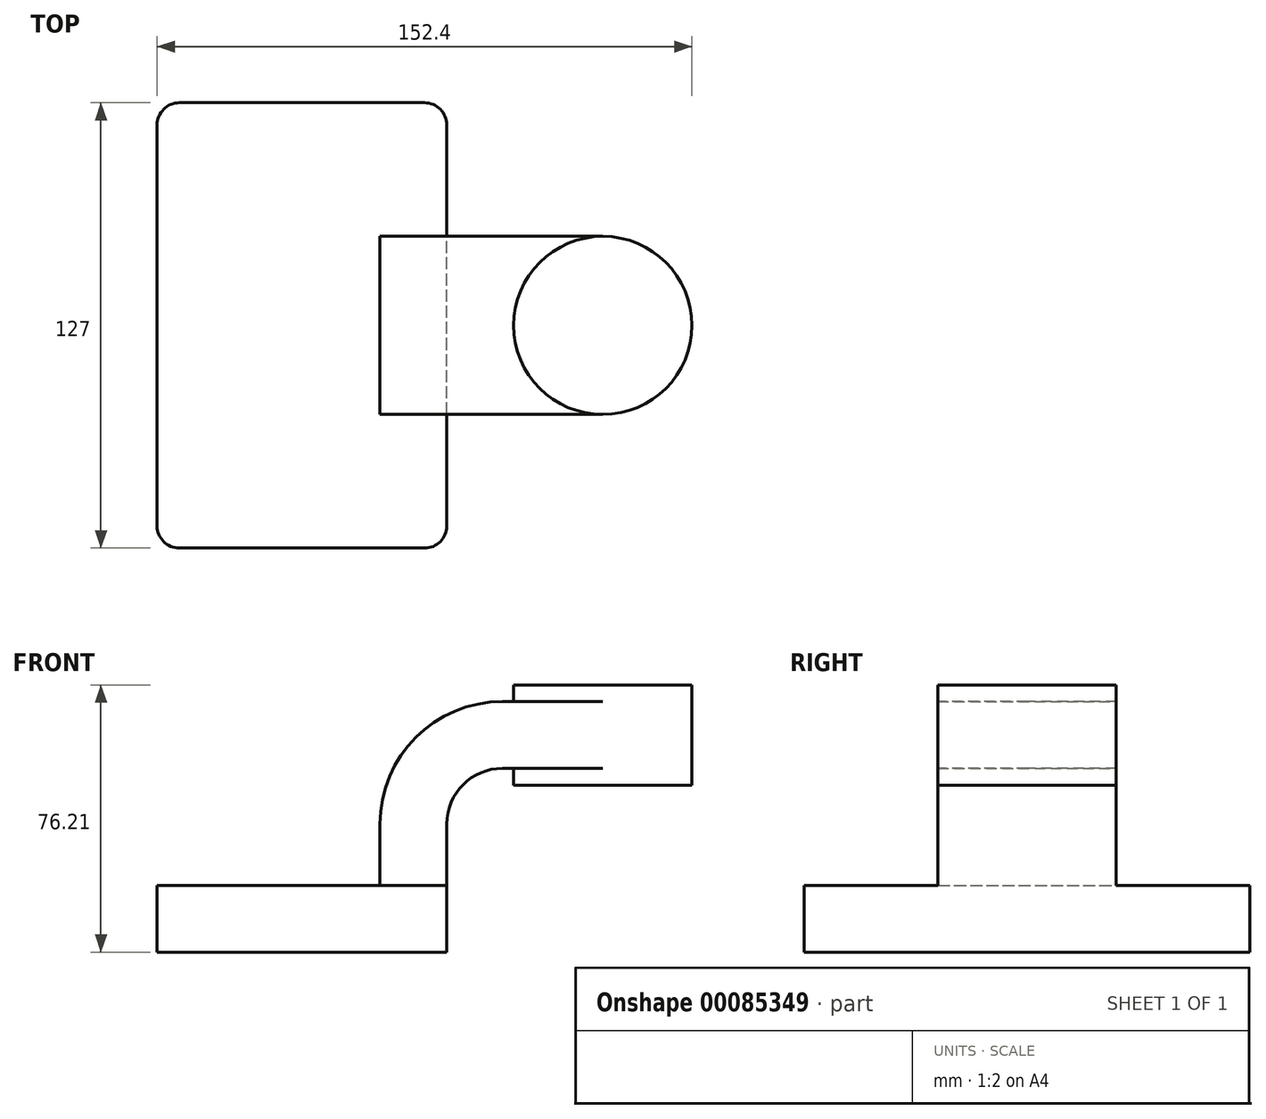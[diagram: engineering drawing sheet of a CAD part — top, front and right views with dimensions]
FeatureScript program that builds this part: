
annotation { "Feature Type Name" : "Feature", "Feature Type Description" : "" }
export const myFeature = defineFeature(function(context is Context, id is Id, definition is map)
    precondition{}
    {
        {
            var Q0;
            Q0=qCreatedBy(makeId("Front.planeOp"),FACE);
            var sketch = newSketch(context, id + "F0", { "sketchPlane" : qUnion([Q0])});
            skLineSegment(sketch, "E0.bottom", {"start": v(41.28, -9.52) * mm, "end": v(-41.28, -9.53) * mm});
            skLineSegment(sketch, "E0.top", {"start": v(41.28, 9.53) * mm, "end": v(-41.28, 9.53) * mm});
            skLineSegment(sketch, "E0.left", {"start": v(41.28, -9.52) * mm, "end": v(41.28, 9.53) * mm});
            skLineSegment(sketch, "E0.right", {"start": v(-41.28, -9.53) * mm, "end": v(-41.28, 9.53) * mm});
            skPoint(sketch, "E0.middle", {"position": v(0, 0) * mm});
            skLineSegment(sketch, "E1.bottom", {"start": v(60.33, 38.1) * mm, "end": v(111.12, 38.1) * mm});
            skLineSegment(sketch, "E1.top", {"start": v(60.32, 66.68) * mm, "end": v(111.12, 66.68) * mm});
            skLineSegment(sketch, "E1.left", {"start": v(60.33, 38.1) * mm, "end": v(60.32, 66.68) * mm});
            skLineSegment(sketch, "E1.right", {"start": v(111.12, 38.1) * mm, "end": v(111.12, 66.68) * mm});
            skPoint(sketch, "E1.middle", {"position": v(85.72, 52.39) * mm});
            skLineSegment(sketch, "E2", {"start": v(41.28, 9.53) * mm, "end": v(41.28, 27) * mm});
            skArc(sketch, "E3", {"start": v(41.27, 27) * mm, "mid": v(45.92, 38.23) * mm, "end": v(57.15, 42.88) * mm});
            skLineSegment(sketch, "E4", {"start": v(57.15, 42.88) * mm, "end": v(85.72, 42.88) * mm});
            skLineSegment(sketch, "E5.0", {"start": v(57.15, 61.93) * mm, "end": v(85.72, 61.93) * mm});
            skArc(sketch, "E5.1", {"start": v(22.23, 27) * mm, "mid": v(32.45, 51.7) * mm, "end": v(57.15, 61.93) * mm});
            skLineSegment(sketch, "E5.2", {"start": v(22.22, 9.53) * mm, "end": v(22.22, 27) * mm});
            skLineSegment(sketch, "E6", {"start": v(85.72, 38.1) * mm, "end": v(85.72, 66.68) * mm});
            skFitSpline(sketch, "E7", {"points": [v(-41.28, 9.53) * mm, v(57.15, 61.93) * mm], "startDerivative": vector(0, 117.26) * mm, "endDerivative": vector(131.4, 0) * mm});
            skPoint(sketch, "E8", {"position": v(-41.28, 0) * mm});
            skSolve(sketch);
        }
        {
            var Q0;
            Q0=makeQuery(id+"F0.imprint","IMPRINT",FACE,{"disambiguationData":[TD([[makeQuery(id+"F0.imprint","IMPRINT",EDGE,{"derivedFrom":sQuery(id+"F0.wireOp",EDGE,"E0.bottom")}),-1.0]])]});
            extrude(context, id + "F1", {"entities" : qUnion([Q0]), "endBound" : BoundingType.SYMMETRIC, "depth" : 127 * mm});
        }
        {
            var Q0;
            {var subQ1=sQuery(id+"F0.wireOp",EDGE,"E2");Q0=makeQuery(id+"F0.imprint","IMPRINT",FACE,{"disambiguationData":[TD([[makeQuery(id+"F0.imprint","IMPRINT",EDGE,{"derivedFrom":subQ1}),1.0]])]});}
            var Q1;
            {var subQ0=sQuery(id+"F0.wireOp",EDGE,"E4");var subQ1=sQuery(id+"F0.wireOp",EDGE,"E1.left");var subQ2=makeQuery(id+"F0.imprint","INTERSECT",VERTEX,{"derivedFrom":[subQ1,subQ0]});Q1=makeQuery(id+"F0.imprint","IMPRINT",FACE,{"disambiguationData":[TD([[makeQuery(id+"F0.imprint","IMPRINT",EDGE,{"disambiguationData":[TD([[subQ2,-1.0]])],"derivedFrom":subQ1}),-1.0]])]});}
            extrude(context, id + "F2", {"entities" : qUnion([Q0, Q1]), "operationType" : NewBodyOperationType.ADD, "endBound" : BoundingType.SYMMETRIC, "depth" : 50.8 * mm});
        }
        {
            var Q0;
            Q0=makeQuery(id+"F0.imprint","IMPRINT",FACE,{"disambiguationData":[TD([[makeQuery(id+"F0.imprint","IMPRINT",EDGE,{"derivedFrom":sQuery(id+"F0.wireOp",EDGE,"E5.1")}),1.0]])]});
            extrude(context, id + "F3", {"entities" : qUnion([Q0]), "operationType" : NewBodyOperationType.ADD, "endBound" : BoundingType.SYMMETRIC, "depth" : 15.88 * mm});
        }
        {
            var Q0;
            {var subQ0=sQuery(id+"F0.wireOp",EDGE,"E1.right");Q0=makeQuery(id+"F0.imprint","IMPRINT",FACE,{"disambiguationData":[TD([[makeQuery(id+"F0.imprint","IMPRINT",EDGE,{"derivedFrom":subQ0}),1.0]])]});}
            var Q1;
            Q1=sQuery(id+"F0.wireOp",EDGE,"E6");
            revolve(context, id + "F4", {"operationType" : NewBodyOperationType.ADD, "entities" : qUnion([Q0]), "axis" : qUnion([Q1]), "revolveType" : RevolveType.FULL});
        }
        {
            var Q0;
            Q0=makeQuery(id+"F1.opExtrude","CAP_EDGE",EDGE,{"disambiguationData":[OSD([sQuery(id+"F0.wireOp",EDGE,"E0.right")])],"isStart":false});
            var Q1;
            Q1=makeQuery(id+"F1.opExtrude","CAP_EDGE",EDGE,{"disambiguationData":[OSD([sQuery(id+"F0.wireOp",EDGE,"E0.left")])],"isStart":false});
            var Q2;
            Q2=makeQuery(id+"F1.opExtrude","CAP_EDGE",EDGE,{"disambiguationData":[OSD([sQuery(id+"F0.wireOp",EDGE,"E0.left")])],"isStart":true});
            var Q3;
            Q3=makeQuery(id+"F1.opExtrude","CAP_EDGE",EDGE,{"disambiguationData":[OSD([sQuery(id+"F0.wireOp",EDGE,"E0.right")])],"isStart":true});
            fillet(context, id + "F5", {"entities" : qUnion([Q0, Q1, Q2, Q3]), "radius" : 6.35 * mm, "tangentPropagation" : true, "allowEdgeOverflow" : false});
        }
    });
